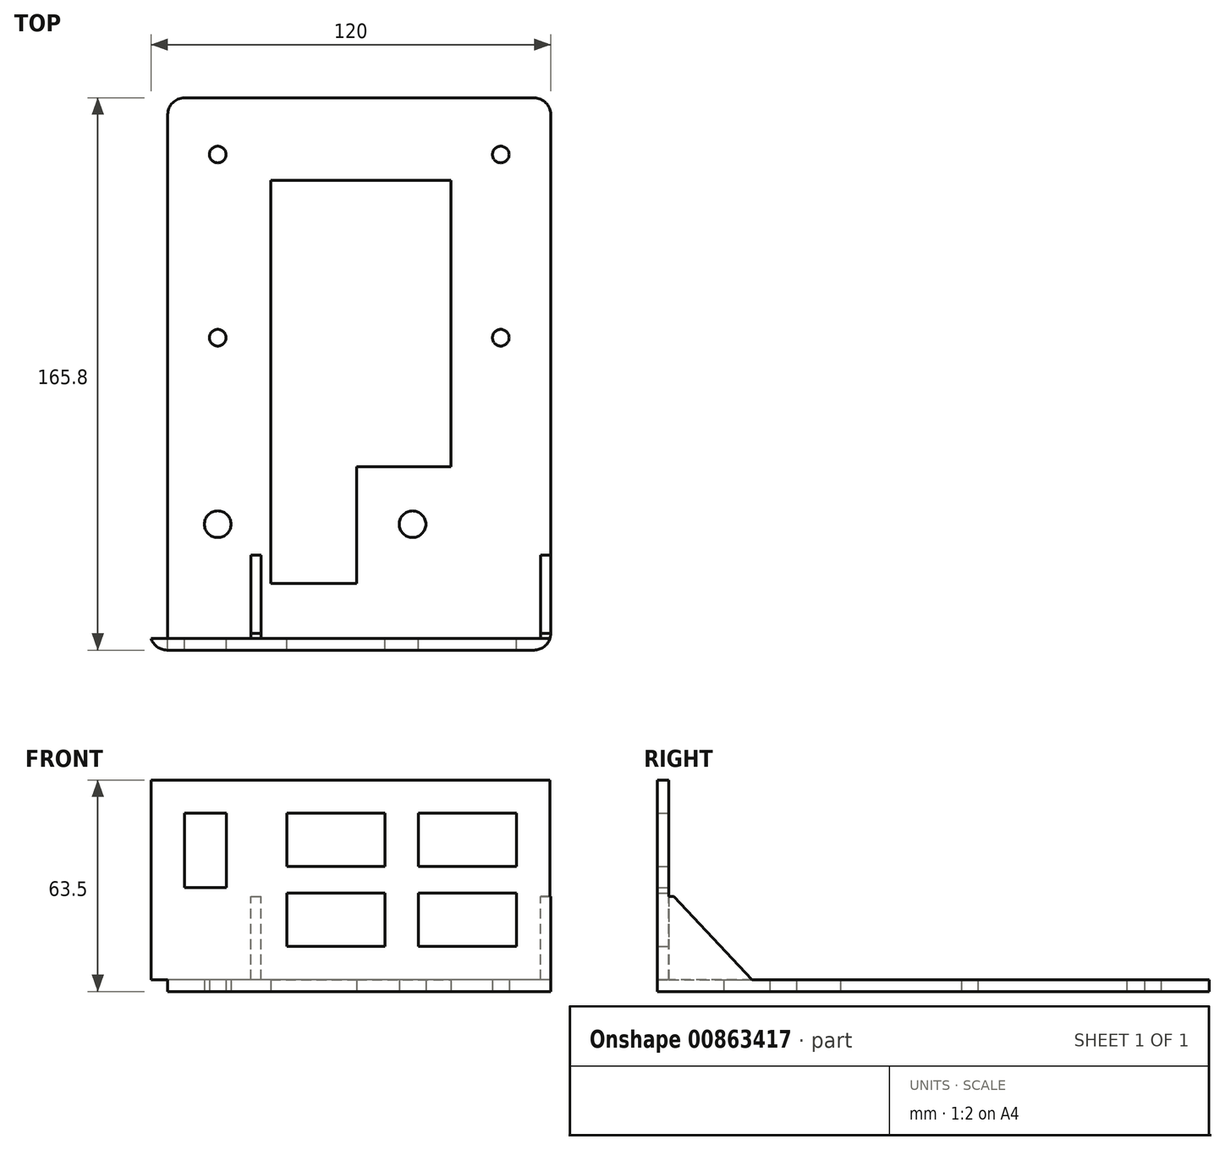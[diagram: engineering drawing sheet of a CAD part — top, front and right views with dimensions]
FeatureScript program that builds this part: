
annotation { "Feature Type Name" : "Feature", "Feature Type Description" : "" }
export const myFeature = defineFeature(function(context is Context, id is Id, definition is map)
    precondition{}
    {
        {
            var Q0;
            Q0=qCreatedBy(makeId("Top.planeOp"),FACE);
            var sketch = newSketch(context, id + "F0", { "sketchPlane" : qUnion([Q0])});
            skLineSegment(sketch, "E0.bottom", {"start": v(0, 0) * mm, "end": v(-115, 0) * mm});
            skLineSegment(sketch, "E0.top", {"start": v(0, 165.8) * mm, "end": v(-115, 165.8) * mm});
            skLineSegment(sketch, "E0.left", {"start": v(0, 0) * mm, "end": v(0, 165.8) * mm});
            skLineSegment(sketch, "E0.right", {"start": v(-115, 0) * mm, "end": v(-115, 165.8) * mm});
            skCircle(sketch, "E1", {"center": v(-41.5, 37.8) * mm, "radius": 4 * mm});
            skCircle(sketch, "E2", {"center": v(-100, 37.8) * mm, "radius": 4 * mm});
            skCircle(sketch, "E3", {"center": v(-100, 148.8) * mm, "radius": 2.5 * mm});
            skCircle(sketch, "E4", {"center": v(-100, 93.8) * mm, "radius": 2.5 * mm});
            skCircle(sketch, "E5", {"center": v(-15, 148.8) * mm, "radius": 2.5 * mm});
            skCircle(sketch, "E6", {"center": v(-15, 93.8) * mm, "radius": 2.5 * mm});
            skLineSegment(sketch, "E7", {"start": v(-30, 141.04) * mm, "end": v(-84.13, 141.04) * mm});
            skLineSegment(sketch, "E8", {"start": v(-84.13, 141.04) * mm, "end": v(-84.13, 20) * mm});
            skLineSegment(sketch, "E9", {"start": v(-84.13, 20) * mm, "end": v(-58.23, 20) * mm});
            skLineSegment(sketch, "E10", {"start": v(-58.23, 20) * mm, "end": v(-58.23, 55) * mm});
            skLineSegment(sketch, "E11", {"start": v(-58.23, 55) * mm, "end": v(-30, 55) * mm});
            skLineSegment(sketch, "E12", {"start": v(-30, 55) * mm, "end": v(-30, 141.04) * mm});
            skPoint(sketch, "E13.orphan", {"position": v(-35.31, 141.04) * mm});
            skSolve(sketch);
        }
        {
            var Q0;
            Q0=makeQuery(id+"F0.imprint","IMPRINT",FACE,{"disambiguationData":[TD([[makeQuery(id+"F0.imprint","IMPRINT",EDGE,{"derivedFrom":sQuery(id+"F0.wireOp",EDGE,"E0.bottom")}),-1.0]])]});
            extrude(context, id + "F1", {"entities" : qUnion([Q0]), "oppositeDirection" : true, "depth" : 3.5 * mm, "offsetDistance" : 25 * mm});
        }
        {
            var Q0;
            Q0=makeQuery(id+"F1.opExtrude","CAP_FACE",FACE,{"disambiguationData":[OSD([sQuery(id+"F0.wireOp",EDGE,"E0.bottom"),sQuery(id+"F0.wireOp",EDGE,"E0.top"),sQuery(id+"F0.wireOp",EDGE,"E0.left"),sQuery(id+"F0.wireOp",EDGE,"E0.right"),sQuery(id+"F0.wireOp",EDGE,"E1"),sQuery(id+"F0.wireOp",EDGE,"E2"),sQuery(id+"F0.wireOp",EDGE,"E3"),sQuery(id+"F0.wireOp",EDGE,"E4"),sQuery(id+"F0.wireOp",EDGE,"E5"),sQuery(id+"F0.wireOp",EDGE,"E6"),sQuery(id+"F0.wireOp",EDGE,"AMhIYsyM-ouOh-bC3b-tB5I-rpUGRMd0qDAw.bottom"),sQuery(id+"F0.wireOp",EDGE,"AMhIYsyM-ouOh-bC3b-tB5I-rpUGRMd0qDAw.top"),sQuery(id+"F0.wireOp",EDGE,"AMhIYsyM-ouOh-bC3b-tB5I-rpUGRMd0qDAw.left"),sQuery(id+"F0.wireOp",EDGE,"AMhIYsyM-ouOh-bC3b-tB5I-rpUGRMd0qDAw.right")])],"isStart":false});
            var sketch = newSketch(context, id + "F2", { "sketchPlane" : qUnion([Q0])});
            skLineSegment(sketch, "E14.bottom", {"start": v(0, 0) * mm, "end": v(-120, 0) * mm});
            skLineSegment(sketch, "E14.top", {"start": v(0, -3.5) * mm, "end": v(-120, -3.5) * mm});
            skLineSegment(sketch, "E14.left", {"start": v(0, 0) * mm, "end": v(0, -3.5) * mm});
            skLineSegment(sketch, "E14.right", {"start": v(-120, 0) * mm, "end": v(-120, -3.5) * mm});
            skSolve(sketch);
        }
        {
            var Q0;
            Q0=makeQuery(id+"F2.imprint","IMPRINT",FACE,{"disambiguationData":[TD([[makeQuery(id+"F2.imprint","IMPRINT",EDGE,{"derivedFrom":sQuery(id+"F2.wireOp",EDGE,"E14.bottom")}),1.0]])]});
            extrude(context, id + "F3", {"entities" : qUnion([Q0]), "operationType" : NewBodyOperationType.ADD, "depth" : 60 * mm, "offsetDistance" : 25 * mm});
        }
        {
            var Q0;
            Q0=makeQuery(id+"F3.opExtrude","SWEPT_FACE",FACE,{"disambiguationData":[OSD([sQuery(id+"F2.wireOp",EDGE,"E14.top")])]});
            var sketch = newSketch(context, id + "F4", { "sketchPlane" : qUnion([Q0])});
            skLineSegment(sketch, "E15.bottom", {"start": v(0, -3.5) * mm, "end": v(3, -3.5) * mm});
            skLineSegment(sketch, "E15.top", {"start": v(0, -28.5) * mm, "end": v(3, -28.5) * mm});
            skLineSegment(sketch, "E15.left", {"start": v(0, -3.5) * mm, "end": v(0, -28.5) * mm});
            skLineSegment(sketch, "E15.right", {"start": v(3, -3.5) * mm, "end": v(3, -28.5) * mm});
            skLineSegment(sketch, "E16.bottom", {"start": v(90, -3.5) * mm, "end": v(87, -3.5) * mm});
            skLineSegment(sketch, "E16.top", {"start": v(90, -28.5) * mm, "end": v(87, -28.5) * mm});
            skLineSegment(sketch, "E16.left", {"start": v(90, -3.5) * mm, "end": v(90, -28.5) * mm});
            skLineSegment(sketch, "E16.right", {"start": v(87, -3.5) * mm, "end": v(87, -28.5) * mm});
            skPoint(sketch, "E17", {"position": v(90, -3.5) * mm});
            skSolve(sketch);
        }
        {
            var Q0;
            Q0=makeQuery(id+"F4.imprint","IMPRINT",FACE,{"disambiguationData":[TD([[makeQuery(id+"F4.imprint","IMPRINT",EDGE,{"derivedFrom":sQuery(id+"F4.wireOp",EDGE,"E15.bottom")}),-1.0]])]});
            var Q1;
            Q1=makeQuery(id+"F4.imprint","IMPRINT",FACE,{"disambiguationData":[TD([[makeQuery(id+"F4.imprint","IMPRINT",EDGE,{"derivedFrom":sQuery(id+"F4.wireOp",EDGE,"E16.bottom")}),-1.0]])]});
            extrude(context, id + "F5", {"entities" : qUnion([Q0, Q1]), "operationType" : NewBodyOperationType.ADD, "depth" : 25 * mm, "offsetDistance" : 25 * mm});
        }
        {
            var Q0;
            Q0=makeQuery(id+"F1.opExtrude","SWEPT_EDGE",EDGE,{"disambiguationData":[OSD([sQuery(id+"F0.wireOp",EDGE,"E0.top"),sQuery(id+"F0.wireOp",EDGE,"E0.left")])]});
            var Q1;
            Q1=makeQuery(id+"F1.opExtrude","SWEPT_EDGE",EDGE,{"disambiguationData":[OSD([sQuery(id+"F0.wireOp",EDGE,"E0.top"),sQuery(id+"F0.wireOp",EDGE,"E0.right")])]});
            var Q2;
            Q2=makeQuery(id+"F3.boolean.opBoolean","MERGE",EDGE,{"derivedFrom":[makeQuery(id+"F1.opExtrude","SWEPT_EDGE",EDGE,{"disambiguationData":[OSD([sQuery(id+"F0.wireOp",EDGE,"E0.bottom"),sQuery(id+"F0.wireOp",EDGE,"E0.left")])]}),makeQuery(id+"F3.opExtrude","SWEPT_EDGE",EDGE,{"disambiguationData":[OSD([sQuery(id+"F2.wireOp",EDGE,"E14.bottom"),sQuery(id+"F2.wireOp",EDGE,"E14.left")])]})]});
            var Q3;
            Q3=makeQuery(id+"F3.boolean.opBoolean","MERGE",EDGE,{"derivedFrom":[makeQuery(id+"F1.opExtrude","SWEPT_EDGE",EDGE,{"disambiguationData":[OSD([sQuery(id+"F0.wireOp",EDGE,"E0.bottom"),sQuery(id+"F0.wireOp",EDGE,"E0.right")])]}),makeQuery(id+"F3.opExtrude","SWEPT_EDGE",EDGE,{"disambiguationData":[OSD([sQuery(id+"F2.wireOp",EDGE,"E14.bottom"),sQuery(id+"F2.wireOp",EDGE,"E14.right")])]})]});
            var Q4;
            Q4=makeQuery(id+"F1.opExtrude","SWEPT_EDGE",EDGE,{"disambiguationData":[OSD([sQuery(id+"F0.wireOp",EDGE,"AMhIYsyM-ouOh-bC3b-tB5I-rpUGRMd0qDAw.bottom"),sQuery(id+"F0.wireOp",EDGE,"AMhIYsyM-ouOh-bC3b-tB5I-rpUGRMd0qDAw.right")])]});
            var Q5;
            Q5=makeQuery(id+"F1.opExtrude","SWEPT_EDGE",EDGE,{"disambiguationData":[OSD([sQuery(id+"F0.wireOp",EDGE,"AMhIYsyM-ouOh-bC3b-tB5I-rpUGRMd0qDAw.top"),sQuery(id+"F0.wireOp",EDGE,"AMhIYsyM-ouOh-bC3b-tB5I-rpUGRMd0qDAw.right")])]});
            var Q6;
            Q6=makeQuery(id+"F1.opExtrude","SWEPT_EDGE",EDGE,{"disambiguationData":[OSD([sQuery(id+"F0.wireOp",EDGE,"AMhIYsyM-ouOh-bC3b-tB5I-rpUGRMd0qDAw.top"),sQuery(id+"F0.wireOp",EDGE,"AMhIYsyM-ouOh-bC3b-tB5I-rpUGRMd0qDAw.left")])]});
            var Q7;
            Q7=makeQuery(id+"F1.opExtrude","SWEPT_EDGE",EDGE,{"disambiguationData":[OSD([sQuery(id+"F0.wireOp",EDGE,"AMhIYsyM-ouOh-bC3b-tB5I-rpUGRMd0qDAw.bottom"),sQuery(id+"F0.wireOp",EDGE,"AMhIYsyM-ouOh-bC3b-tB5I-rpUGRMd0qDAw.left")])]});
            fillet(context, id + "F6", {"entities" : qUnion([Q0, Q1, Q2, Q3, Q4, Q5, Q6, Q7]), "radius" : 5 * mm, "tangentPropagation" : true, "allowEdgeOverflow" : false});
        }
        {
            var Q0;
            Q0=makeQuery(id+"F0.imprint","IMPRINT",FACE,{"disambiguationData":[TD([[makeQuery(id+"F0.imprint","IMPRINT",EDGE,{"derivedFrom":sQuery(id+"F0.wireOp",EDGE,"E0.bottom")}),-1.0]])]});
            var sketch = newSketch(context, id + "F7", { "sketchPlane" : qUnion([Q0])});
            skLineSegment(sketch, "E18.top", {"start": v(-115.06, 0) * mm, "end": v(-110.06, 0) * mm});
            skLineSegment(sketch, "E18.left", {"start": v(-115.06, 165.8) * mm, "end": v(-115.06, 0) * mm});
            skLineSegment(sketch, "E18.right", {"start": v(-110.06, 165.8) * mm, "end": v(-110.06, 0) * mm});
            skLineSegment(sketch, "E19.bottom", {"start": v(0, 165.8) * mm, "end": v(-5, 165.8) * mm});
            skLineSegment(sketch, "E19.top", {"start": v(0, 0) * mm, "end": v(-5, 0) * mm});
            skLineSegment(sketch, "E19.left", {"start": v(0, 165.8) * mm, "end": v(0, 0) * mm});
            skLineSegment(sketch, "E19.right", {"start": v(-5, 165.8) * mm, "end": v(-5, 0) * mm});
            skLineSegment(sketch, "E20.top", {"start": v(-115.06, 165.8) * mm, "end": v(-115.06, 165.8) * mm});
            skLineSegment(sketch, "E21", {"start": v(-115.06, 165.8) * mm, "end": v(-110.06, 165.8) * mm});
            skSolve(sketch);
        }
        {
            var Q0;
            Q0=makeQuery(id+"F1.opExtrude","SWEPT_BODY",BODY,{"disambiguationData":[OSD([sQuery(id+"F0.wireOp",EDGE,"E0.bottom"),sQuery(id+"F0.wireOp",EDGE,"E0.top"),sQuery(id+"F0.wireOp",EDGE,"E0.left"),sQuery(id+"F0.wireOp",EDGE,"E0.right"),sQuery(id+"F0.wireOp",EDGE,"E1"),sQuery(id+"F0.wireOp",EDGE,"E2"),sQuery(id+"F0.wireOp",EDGE,"E3"),sQuery(id+"F0.wireOp",EDGE,"E4"),sQuery(id+"F0.wireOp",EDGE,"E5"),sQuery(id+"F0.wireOp",EDGE,"E6"),sQuery(id+"F0.wireOp",EDGE,"E7"),sQuery(id+"F0.wireOp",EDGE,"E8"),sQuery(id+"F0.wireOp",EDGE,"E9"),sQuery(id+"F0.wireOp",EDGE,"E10"),sQuery(id+"F0.wireOp",EDGE,"E11"),sQuery(id+"F0.wireOp",EDGE,"E12")])]});
            var Q1;
            Q1=makeQuery(id+"F7.imprint","IMPRINT",FACE,{"disambiguationData":[TD([[makeQuery(id+"F7.imprint","IMPRINT",EDGE,{"derivedFrom":sQuery(id+"F7.wireOp",EDGE,"E19.bottom")}),1.0]])]});
            mirror(context, id + "F8", {"entities" : qUnion([Q0]), "mirrorPlane" : qUnion([Q1])});
        }
        {
            var Q0;
            Q0=makeQuery(id+"F1.opExtrude","SWEPT_BODY",BODY,{"disambiguationData":[OSD([sQuery(id+"F0.wireOp",EDGE,"E0.bottom"),sQuery(id+"F0.wireOp",EDGE,"E0.top"),sQuery(id+"F0.wireOp",EDGE,"E0.left"),sQuery(id+"F0.wireOp",EDGE,"E0.right"),sQuery(id+"F0.wireOp",EDGE,"E1"),sQuery(id+"F0.wireOp",EDGE,"E2"),sQuery(id+"F0.wireOp",EDGE,"E3"),sQuery(id+"F0.wireOp",EDGE,"E4"),sQuery(id+"F0.wireOp",EDGE,"E5"),sQuery(id+"F0.wireOp",EDGE,"E6"),sQuery(id+"F0.wireOp",EDGE,"E7"),sQuery(id+"F0.wireOp",EDGE,"E8"),sQuery(id+"F0.wireOp",EDGE,"E9"),sQuery(id+"F0.wireOp",EDGE,"E10"),sQuery(id+"F0.wireOp",EDGE,"E11"),sQuery(id+"F0.wireOp",EDGE,"E12")])]});
            deleteBodies(context, id + "F9", {"entities" : qUnion([Q0])});
        }
        {
            var Q0;
            Q0=makeQuery(id+"F8.opPattern","COPY",EDGE,{"derivedFrom":makeQuery(id+"F3.opExtrude","SWEPT_EDGE",EDGE,{"disambiguationData":[OSD([sQuery(id+"F2.wireOp",EDGE,"E14.bottom"),sQuery(id+"F2.wireOp",EDGE,"E14.right")])]}),"instanceName":"1"});
            fillet(context, id + "F10", {"entities" : qUnion([Q0]), "radius" : 5 * mm, "tangentPropagation" : true, "allowEdgeOverflow" : false});
        }
        {
            var Q0;
            Q0=makeQuery(id+"F8.opPattern","COPY",FACE,{"derivedFrom":makeQuery(id+"F5.boolean.opBoolean","MERGE",FACE,{"derivedFrom":[makeQuery(id+"F3.boolean.opBoolean","MERGE",FACE,{"derivedFrom":[makeQuery(id+"F1.opExtrude","SWEPT_FACE",FACE,{"disambiguationData":[OSD([sQuery(id+"F0.wireOp",EDGE,"E0.left")])]}),makeQuery(id+"F3.opExtrude","SWEPT_FACE",FACE,{"disambiguationData":[OSD([sQuery(id+"F2.wireOp",EDGE,"E14.left")])]})]}),makeQuery(id+"F5.opExtrude","SWEPT_FACE",FACE,{"disambiguationData":[OSD([sQuery(id+"F4.wireOp",EDGE,"E15.left")])]})]}),"instanceName":"1"});
            var sketch = newSketch(context, id + "F11", { "sketchPlane" : qUnion([Q0])});
            skLineSegment(sketch, "E22", {"start": v(28.5, 3.5) * mm, "end": v(5, 28.5) * mm});
            skSolve(sketch);
        }
        {
            var Q0;
            Q0=makeQuery(id+"F11.imprint","IMPRINT",FACE,{"disambiguationData":[TD([[makeQuery(id+"F11.imprint","IMPRINT",EDGE,{"derivedFrom":sQuery(id+"F11.wireOp",EDGE,"E22")}),-1.0]])]});
            extrude(context, id + "F12", {"entities" : qUnion([Q0]), "operationType" : NewBodyOperationType.REMOVE, "endBound" : BoundingType.THROUGH_ALL, "oppositeDirection" : true, "depth" : 25 * mm, "offsetDistance" : 25 * mm});
        }
        {
            var Q0;
            Q0=makeQuery(id+"F8.opPattern","COPY",FACE,{"derivedFrom":makeQuery(id+"F3.opExtrude","SWEPT_FACE",FACE,{"disambiguationData":[OSD([sQuery(id+"F2.wireOp",EDGE,"E14.top")])]}),"instanceName":"1"});
            var sketch = newSketch(context, id + "F13", { "sketchPlane" : qUnion([Q0])});
            skLineSegment(sketch, "E23", {"start": v(140.1, 3.5) * mm, "end": v(140.1, 19.5) * mm, "construction": true});
            skLineSegment(sketch, "E24", {"start": v(140.1, 19.5) * mm, "end": v(-50.67, 19.5) * mm, "construction": true});
            skLineSegment(sketch, "E25", {"start": v(10.23, 13.5) * mm, "end": v(79.23, 13.5) * mm});
            skLineSegment(sketch, "E26", {"start": v(79.23, 53.5) * mm, "end": v(10.23, 53.5) * mm});
            skLineSegment(sketch, "E27", {"start": v(97.38, 53.5) * mm, "end": v(97.38, 31.24) * mm});
            skLineSegment(sketch, "E28", {"start": v(97.38, 31.24) * mm, "end": v(110, 31.24) * mm});
            skLineSegment(sketch, "E29", {"start": v(110, 31.24) * mm, "end": v(110, 53.5) * mm});
            skLineSegment(sketch, "E30", {"start": v(110, 53.5) * mm, "end": v(97.38, 53.5) * mm});
            skLineSegment(sketch, "E31", {"start": v(49.73, 53.5) * mm, "end": v(49.73, 13.5) * mm});
            skLineSegment(sketch, "E32", {"start": v(10.23, 53.5) * mm, "end": v(10.23, 13.5) * mm});
            skLineSegment(sketch, "E33", {"start": v(79.23, 53.5) * mm, "end": v(79.23, 13.5) * mm});
            skLineSegment(sketch, "E34", {"start": v(39.73, 53.5) * mm, "end": v(39.73, 13.5) * mm});
            skLineSegment(sketch, "E35", {"start": v(10.23, 37.5) * mm, "end": v(39.73, 37.5) * mm});
            skLineSegment(sketch, "E36", {"start": v(10.23, 29.5) * mm, "end": v(39.73, 29.5) * mm});
            skLineSegment(sketch, "E37", {"start": v(49.73, 37.5) * mm, "end": v(79.23, 37.5) * mm});
            skLineSegment(sketch, "E38", {"start": v(49.73, 29.5) * mm, "end": v(79.23, 29.5) * mm});
            skSolve(sketch);
        }
        {
            var Q0;
            {var subQ5=sQuery(id+"F13.wireOp",EDGE,"E35");Q0=makeQuery(id+"F13.imprint","IMPRINT",FACE,{"disambiguationData":[TD([[makeQuery(id+"F13.imprint","IMPRINT",EDGE,{"derivedFrom":subQ5}),1.0]])]});}
            var Q1;
            {var subQ5=sQuery(id+"F13.wireOp",EDGE,"E37");Q1=makeQuery(id+"F13.imprint","IMPRINT",FACE,{"disambiguationData":[TD([[makeQuery(id+"F13.imprint","IMPRINT",EDGE,{"derivedFrom":subQ5}),1.0]])]});}
            var Q2;
            {var subQ5=sQuery(id+"F13.wireOp",EDGE,"E38");Q2=makeQuery(id+"F13.imprint","IMPRINT",FACE,{"disambiguationData":[TD([[makeQuery(id+"F13.imprint","IMPRINT",EDGE,{"derivedFrom":subQ5}),-1.0]])]});}
            var Q3;
            {var subQ5=sQuery(id+"F13.wireOp",EDGE,"E36");Q3=makeQuery(id+"F13.imprint","IMPRINT",FACE,{"disambiguationData":[TD([[makeQuery(id+"F13.imprint","IMPRINT",EDGE,{"derivedFrom":subQ5}),-1.0]])]});}
            var Q4;
            Q4=makeQuery(id+"F13.imprint","IMPRINT",FACE,{"disambiguationData":[TD([[makeQuery(id+"F13.imprint","IMPRINT",EDGE,{"derivedFrom":sQuery(id+"F13.wireOp",EDGE,"E27")}),1.0]])]});
            extrude(context, id + "F14", {"entities" : qUnion([Q0, Q1, Q2, Q3, Q4]), "operationType" : NewBodyOperationType.REMOVE, "endBound" : BoundingType.UP_TO_NEXT, "oppositeDirection" : true, "depth" : 25 * mm, "offsetDistance" : 25 * mm});
        }
    });
